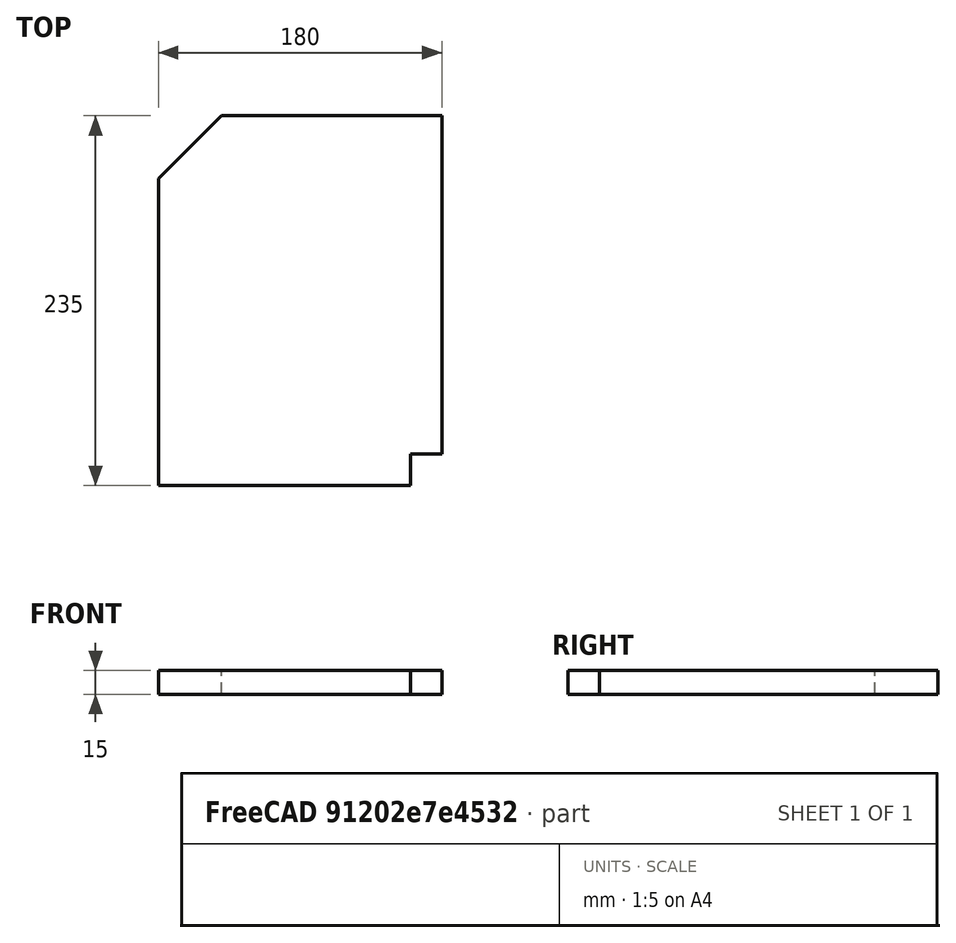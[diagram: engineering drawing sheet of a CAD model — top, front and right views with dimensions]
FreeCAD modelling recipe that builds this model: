
FCSTD DOCUMENT  (FreeCAD 0.18R4 (GitTag))
Label: LeftSide-B
License: All rights reserved
LicenseURL: http://en.wikipedia.org/wiki/All_rights_reserved
objects: Sketcher::SketchObject×1, PartDesign::Pad×1, PartDesign::Body×1, App::Part×1
note: 4 computed .brp shape members not serialized (recipe doc carries the construction recipe); baked Part::Feature solids carry a one-line shape summary decoded from their .brp

FEATURE [Sketcher::SketchObject] CopySketch  label="Sketch"
  MapMode = 5
  Support = -> [XY_Plane001]
  sketch-geometry (7):
    g0: LineSegment StartX=-180 StartY=1.3e-15 StartZ=0 EndX=-180 EndY=195 EndZ=0
    g1: LineSegment StartX=-180 StartY=195 StartZ=0 EndX=-140 EndY=235 EndZ=0
    g2: LineSegment StartX=-140 StartY=235 StartZ=0 EndX=0 EndY=235 EndZ=0
    g3: LineSegment StartX=-20 StartY=1.3e-15 StartZ=0 EndX=-20 EndY=20 EndZ=0
    g4: LineSegment StartX=-20 StartY=20 StartZ=0 EndX=0 EndY=20 EndZ=0
    g5: LineSegment StartX=0 StartY=235 StartZ=0 EndX=0 EndY=20 EndZ=0
    g6: LineSegment StartX=-20 StartY=1.3e-15 StartZ=0 EndX=-180 EndY=1.3e-15 EndZ=0
  constraints (21):
    c: Coincident(g0,g1)
    c: Coincident(g1,g2)
    c: Vertical(g0)
    c: Horizontal(g2)
    c: Distance(g0) = 195
    c: Distance(g2) = 140
    c: Coincident(g3,g4)
    c: Vertical(g3)
    c: Horizontal(g4)
    c: Distance(g4) = 20
    c: Distance(g3) = 20
    c: Distance(g5) = 215
    c: Vertical(g5)
    c: Coincident(g2,g5)
    c: Horizontal(g6)
    c: Coincident(g0,g6)
    c: Coincident(g5,g4)
    c: Distance(g6) = 160
    c: Distance(g-1,g3) = 20
    c: Distance(g-1,g4) = 20
    c: Coincident(g6,g3)
FEATURE [PartDesign::Pad] Pad
  Length = 15
  Length2 = 100
  Profile = -> CopySketch
  Type = 0
FEATURE [PartDesign::Body] Body  label="Side"
  Group = -> [CopySketch,Pad]
  Origin = -> Origin001
  Tip = -> Pad
FEATURE [App::Part] Part
  Group = -> [Body]
  Origin = -> Origin
